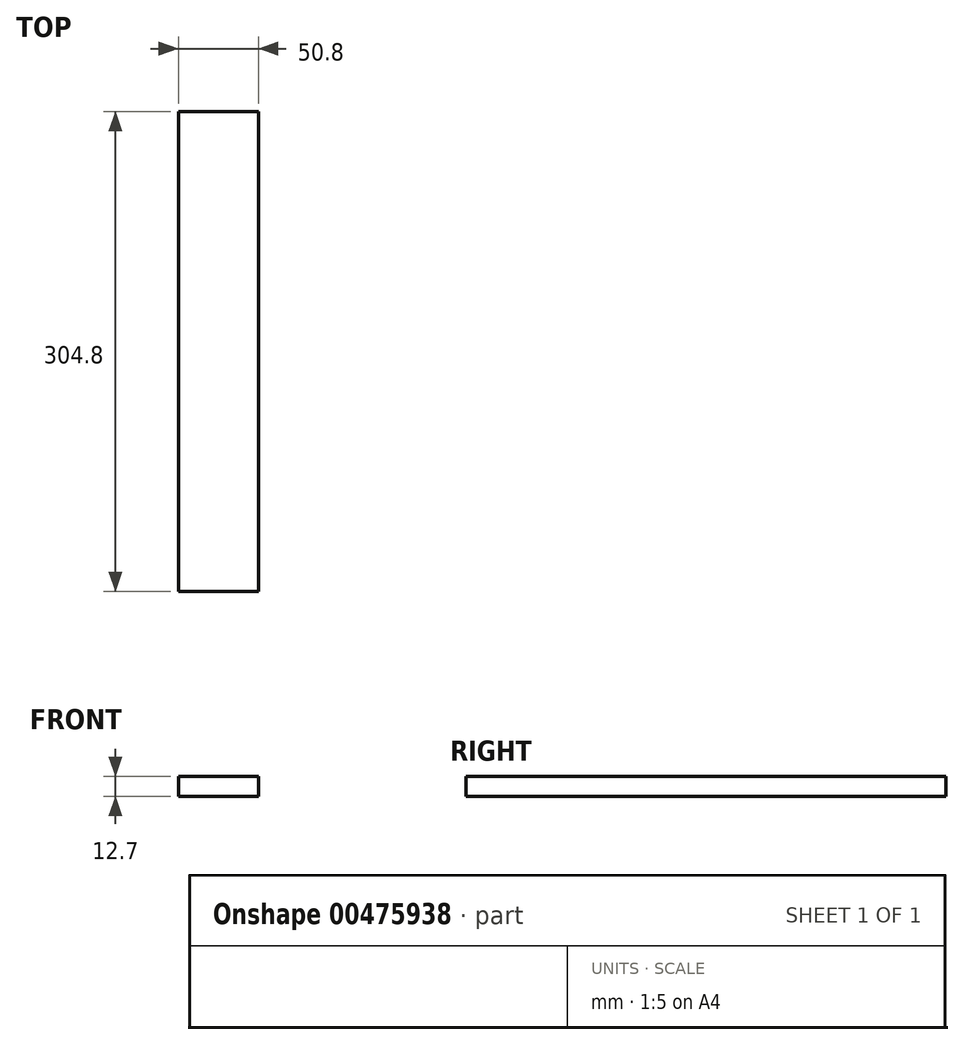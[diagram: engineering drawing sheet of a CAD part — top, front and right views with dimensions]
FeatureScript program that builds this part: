
annotation { "Feature Type Name" : "Feature", "Feature Type Description" : "" }
export const myFeature = defineFeature(function(context is Context, id is Id, definition is map)
    precondition{}
    {
        {
            var Q0;
            Q0=qCreatedBy(makeId("Top.planeOp"),FACE);
            var sketch = newSketch(context, id + "F0", { "sketchPlane" : qUnion([Q0])});
            skLineSegment(sketch, "E0.bottom", {"start": v(0, 0) * mm, "end": v(-50.8, 0) * mm});
            skLineSegment(sketch, "E0.top", {"start": v(0, 304.8) * mm, "end": v(-50.8, 304.8) * mm});
            skLineSegment(sketch, "E0.left", {"start": v(0, 0) * mm, "end": v(0, 304.8) * mm});
            skLineSegment(sketch, "E0.right", {"start": v(-50.8, 0) * mm, "end": v(-50.8, 304.8) * mm});
            skPoint(sketch, "E0.middle", {"position": v(-25.4, 152.4) * mm});
            skSolve(sketch);
        }
        {
            var Q0;
            Q0=makeQuery(id+"F0.imprint","IMPRINT",FACE,{"disambiguationData":[TD([[makeQuery(id+"F0.imprint","IMPRINT",EDGE,{"derivedFrom":sQuery(id+"F0.wireOp",EDGE,"E0.bottom")}),-1.0]])]});
            extrude(context, id + "F1", {"entities" : qUnion([Q0]), "depth" : 12.7 * mm});
        }
    });
